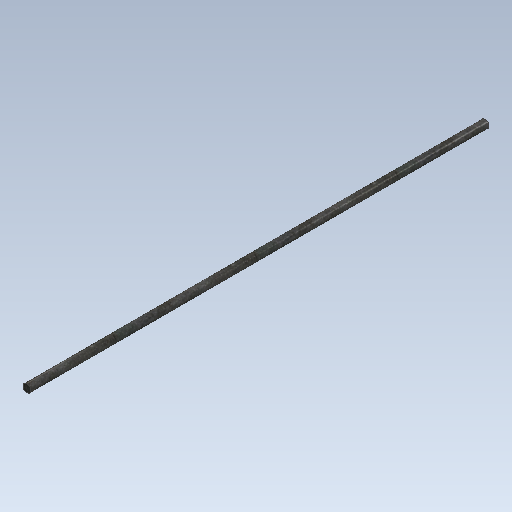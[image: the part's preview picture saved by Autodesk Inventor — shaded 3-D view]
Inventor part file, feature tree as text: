
AUTODESK INVENTOR PART (.ipt)
format: ipt  version: 2020 (Build 240168000, 168)  size: 87,552 bytes
history: native  units: mm
features: extrude x1, sketch x1
ambient origin geometry x8: Origin, YZ Plane, XZ Plane, XY Plane, X Axis, Y Axis, Z Axis, Center Point
bodies: Solid1 (feature_tree)
feature tree (2):
  extrude  "Extrusion1"  Depth=570.0mm TaperAngle=0.0deg
  sketch  "Sketch1"  dims[d0=10.0mm d1=570.0mm d2=0.0mm]
